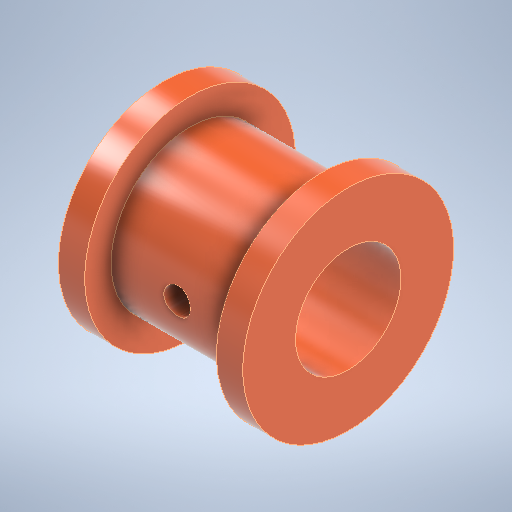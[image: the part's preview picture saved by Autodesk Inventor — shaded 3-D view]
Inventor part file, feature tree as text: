
AUTODESK INVENTOR PART (.ipt)
format: ipt  version: 2025.1 (Build 291241000, 241)  size: 322,560 bytes
history: native  units: mm
features: sketch x3, hole x2, revolve x1, plane x1
ambient origin geometry x8: Origin, YZ Plane, XZ Plane, XY Plane, X Axis, Y Axis, Z Axis, Center Point
bodies: Solid1 (feature_tree)
feature tree (7):
  revolve  "Revolution1"  [1 undecoded]
  plane  "Work Plane1"
  sketch  "Sketch3"  dims[d4=2.0mm d5=5.0mm d6=90.0deg d7=8.0mm d8=6.0mm d9=4.0mm d10=2.0mm d11=90.0deg d12=6.0mm d13=0.0mm d14=6.0mm d15=2.0mm d16=6.0mm d17=4.0mm d18=2.0mm d19=90.0deg d20=8.0mm d21=0.0mm]
  hole  "Hole1"  [1 undecoded]
  hole  "Hole2"  [1 undecoded]
  sketch  "Sketch1"  dims[d0=10.0mm d1=16.0mm]
  sketch  "Sketch2"  dims[d2=12.0mm d3=2.0mm]
note: 3 required parameter values undecoded (feature->parameter linkage not recoverable at this tier; creation-order binding heuristic only, values carry confidence <= 0.55)